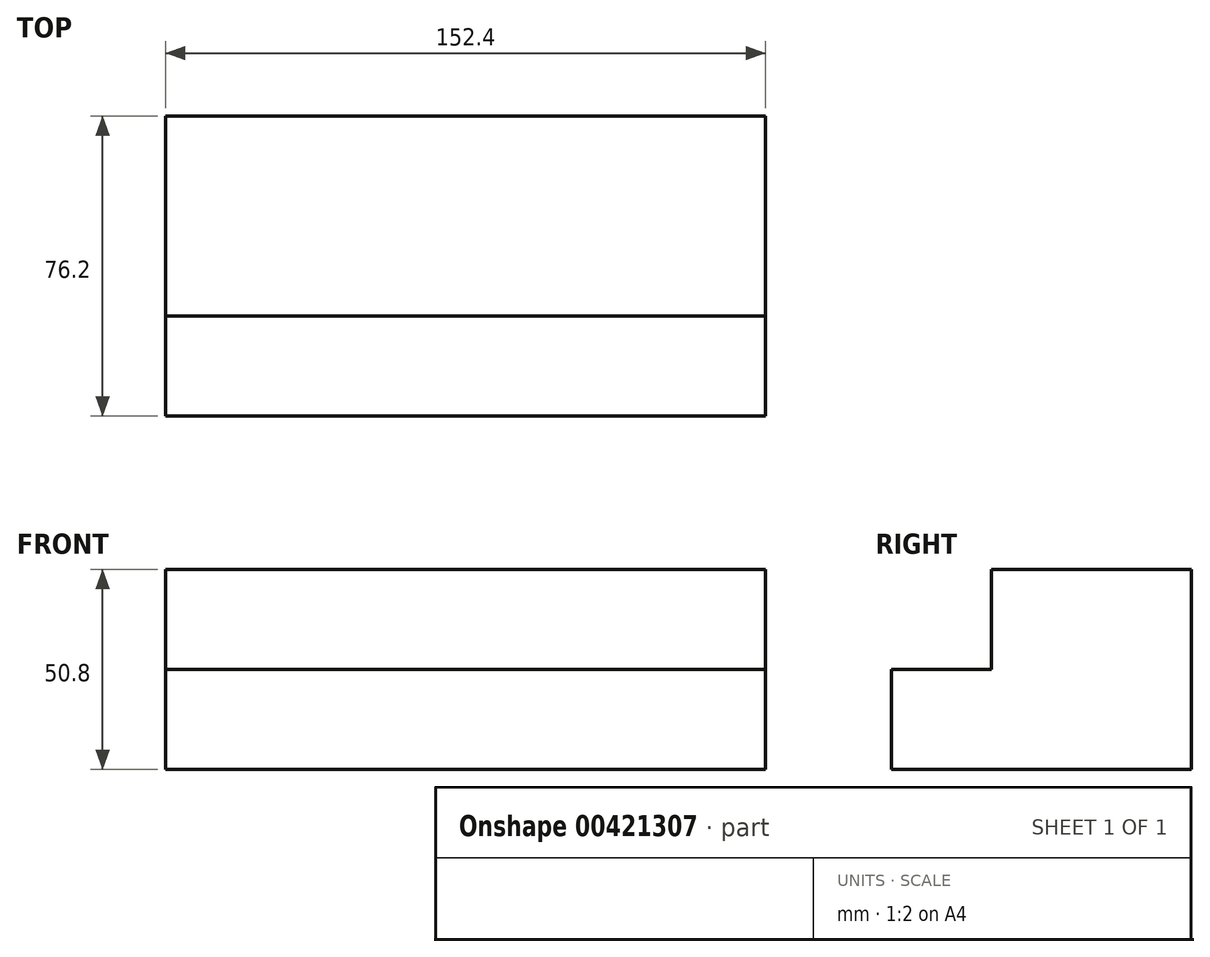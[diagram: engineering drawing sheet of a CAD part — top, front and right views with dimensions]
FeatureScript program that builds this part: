
annotation { "Feature Type Name" : "Feature", "Feature Type Description" : "" }
export const myFeature = defineFeature(function(context is Context, id is Id, definition is map)
    precondition{}
    {
        {
            var Q0;
            Q0=qCreatedBy(makeId("Right.planeOp"),FACE);
            var sketch = newSketch(context, id + "F0", { "sketchPlane" : qUnion([Q0])});
            skLineSegment(sketch, "E0", {"start": v(0, 0) * mm, "end": v(0, 25.4) * mm});
            skLineSegment(sketch, "E1", {"start": v(0, 25.4) * mm, "end": v(25.4, 25.4) * mm});
            skLineSegment(sketch, "E2", {"start": v(25.4, 25.4) * mm, "end": v(25.4, 50.8) * mm});
            skLineSegment(sketch, "E3", {"start": v(25.4, 50.8) * mm, "end": v(76.2, 50.8) * mm});
            skLineSegment(sketch, "E4", {"start": v(76.2, 50.8) * mm, "end": v(76.2, 0) * mm});
            skLineSegment(sketch, "E5", {"start": v(76.2, 0) * mm, "end": v(0, 0) * mm});
            skSolve(sketch);
        }
        {
            var Q0;
            Q0=makeQuery(id+"F0.imprint","IMPRINT",FACE,{"disambiguationData":[TD([[makeQuery(id+"F0.imprint","IMPRINT",EDGE,{"derivedFrom":sQuery(id+"F0.wireOp",EDGE,"E0")}),-1.0]])]});
            extrude(context, id + "F1", {"entities" : qUnion([Q0]), "depth" : 152.4 * mm});
        }
    });
